# Revit family: rba-bim-B532
name_source: partatom
category: Generic Models
revit_build: Autodesk Revit 2018 (Build: 20170223_1515(x64)
units: mm (PartAtom-declared; Revit-internal decimal feet)

## family parameters
Always vertical = No
Can host rebar = No
Cut with Voids When Loaded = No
OmniClass Number = 23.40.20.21.17
OmniClass Title = Paper Towel Dispensers, Disposal Units
Part Type = Normal
Room Calculation Point = No
Round Connector Dimension = Use Diameter
Shared = Yes
Work Plane-Based = No

## types (1)
- B532
    Assembly Code = E2020200
    Description = Countertop Mounted Circular Waste Chute, Satin
    Keynote = Satin-finish stainless steel. Flat flange suitable for counter, recessed or under-counter installation. Provides access to under-counter waste receptacle (not included). Outer Dia 6-3/16" (173mm), Inner Dia 5-5/16" (151mm), Recess 3-7/8" (98mm).
    Manufacturer = Bobrick Washroom Equipment, Inc.
    Materials and Finishes = Satin Finish Stainless Steel
    Model = B532
    Modified Issue = 20220323.01
    Product URL = http://www.bobrick.com
    Revised Date = 5/28/2015
    URL = http://www.bobrick.com

## geometry (parser evidence)
native form markers: Blend x8, Sweep x1
no freeform markers — native parametric forms only
